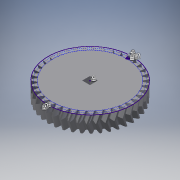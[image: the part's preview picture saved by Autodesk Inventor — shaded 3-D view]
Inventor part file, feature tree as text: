
AUTODESK INVENTOR PART (.ipt)
format: ipt  version: 2017 (Build 210142000, 142)  size: 1,054,720 bytes
history: native  units: mm
features: sketch x3, extrude x3, pattern_circular x2, helix x2, projected_geometry x1
ambient origin geometry x8: Origin, YZ Plane, XZ Plane, XY Plane, X Axis, Y Axis, Z Axis, Center Point
bodies: Solid1 (feature_tree)
feature tree (11):
  sketch  "Sketch1"  dims[d0=20.0mm d1=0.0mm]
  extrude  "Extrusion1"  TaperAngle=0.0deg  [1 undecoded]
  extrude  "Extrusion2"  Depth=390.0mm TaperAngle=360.0deg
  pattern_circular  "Circular Pattern1"  [2 undecoded]
  extrude  "Extrusion3"  Depth=390.0mm TaperAngle=360.0deg
  helix  "Coil1"  [1 undecoded]
  helix  "Coil2"  [1 undecoded]
  pattern_circular  "Circular Pattern2"  [2 undecoded]
  sketch  "Sketch2"  dims[d2=10.0mm d3=0.0mm d4=390.0mm d5=360.0deg]
  sketch  "Sketch3"  dims[d7=9.525mm d8=10.0mm d9=0.0mm d10=10.0mm d11=10.0mm d12=0.1mm d13=0.0mm d14=90.0deg d15=90.0deg d16=0.0mm d17=0.0mm d18=10.0mm d19=10.0mm d20=0.1mm d21=0.0mm d22=90.0deg d23=90.0deg d24=0.0mm d25=0.0mm d26=390.0mm d27=360.0deg]
  projected_geometry  "Projected Loop1"
note: 7 required parameter values undecoded (feature->parameter linkage not recoverable at this tier; creation-order binding heuristic only, values carry confidence <= 0.55)
